# Revit family: 2M_Relief Valve_UNIVAL_URLV-0301 - 50-200 mm
name_source: partatom
category: Pipe Accessories
revit_build: Autodesk Revit 2016 (Build: 20150220_1215(x64)
units: mm (PartAtom-declared; Revit-internal decimal feet)

## family parameters
Always vertical = Yes
Cut with Voids When Loaded = No
OmniClass Number = 23.65.55.14
OmniClass Title = Valves for Liquid Services
Part Type = Valve - Breaks Into
Round Connector Dimension = Use Diameter
Shared = No
Work Plane-Based = No

## types (7) — shared parameters
Body Material = Ductile iron
Certifications = CE
Color = UNIVAL_Red
Connection Type = Flanged / Grooved
Description = Relief valve
Description TR = Relief vana
Disc Material = EPDM
Flanged = Yes
Grooved = No
Loss Method = Not Defined
Manufacturer = Giacomini Unival
Giacomini Unival
Giacomini Unival
Max. Working Temperature = 90°C
Pressure Rating = PN16 / PN25
URL = http://www.unival.com.tr

## per-type parameters (varying)
| type | D | DN | Elbow_D | Elbow_curve | Elbow_dist | Elbow_h | Ext_dist | Flange_w | H | H1 | Hexagon_d | Hexagon_h | Kv | L | Model | Profile2_x | Profile_d | Profile_y | Top_D |
| DN50 | 163 mm | 50 mm | 64 mm  [stored 0.209974 ft] | 120 mm | 89 mm | 60 mm  [stored 0.19685 ft] | 5 mm  [stored 0.0164042 ft] | 17 mm | 149 mm | 68 mm  [stored 0.223097 ft] | 63 mm  [stored 0.206693 ft] | 15 mm  [stored 0.0492126 ft] | 102 | 212 mm | URLV-0301X050 | 71 mm | 24 mm  [stored 0.0787402 ft] | 50 mm  [stored 0.164042 ft] | 32 mm  [stored 0.104987 ft] |
| DN65 | 184 mm | 65 mm | 65 mm  [stored 0.213255 ft] | 116 mm | 93 mm | 58 mm  [stored 0.190289 ft] | 5 mm  [stored 0.0164042 ft] | 17 mm | 154 mm | 66 mm  [stored 0.216535 ft] | 66 mm  [stored 0.216535 ft] | 15 mm  [stored 0.0492126 ft] | 102 | 220 mm | URLV-0301X065 | 73 mm  [stored 0.239501 ft] | 31 mm | 55 mm  [stored 0.180446 ft] | 33 mm  [stored 0.108268 ft] |
| DN80 | 204 mm | 80 mm | 80 mm  [stored 0.262467 ft] | 130 mm | 126 mm | 65 mm  [stored 0.213255 ft] | 33 mm  [stored 0.108268 ft] | 17 mm | 173 mm | 73 mm  [stored 0.239501 ft] | 80 mm  [stored 0.262467 ft] | 15 mm  [stored 0.0492126 ft] | 201 | 286 mm | URLV-0301X080 | 95 mm | 38 mm  [stored 0.124672 ft] | 62 mm  [stored 0.203412 ft] | 40 mm  [stored 0.131234 ft] |
| DN100 | 210 mm | 100 mm | 100 mm | 130 mm | 148 mm | 65 mm  [stored 0.213255 ft] | 40 mm  [stored 0.131234 ft] | 17 mm | 173 mm | 73 mm  [stored 0.239501 ft] | 100 mm | 15 mm  [stored 0.0492126 ft] | 216 | 330 mm | URLV-0301X100 | 110 mm | 48 mm  [stored 0.15748 ft] | 70 mm  [stored 0.229659 ft] | 50 mm  [stored 0.164042 ft] |
| DN125 | 262 mm | 125 mm | 125 mm | 160 mm | 167 mm | 80 mm  [stored 0.262467 ft] | 42 mm  [stored 0.137795 ft] | 17 mm | 212 mm | 88 mm  [stored 0.288714 ft] | 114 mm | 15 mm  [stored 0.0492126 ft] | 216 | 368 mm | URLV-0301X125 | 123 mm | 60 mm  [stored 0.19685 ft] | 86 mm  [stored 0.282152 ft] | 57 mm  [stored 0.187008 ft] |
| DN150 | 288 mm | 150 mm | 150 mm | 295 mm | 180 mm | 148 mm | 5 mm  [stored 0.0164042 ft] | 17 mm | 325 mm | 156 mm | 110 mm | 30 mm  [stored 0.0984252 ft] | 484 | 394 mm | URLV-0301X150 | 131 mm | 72 mm  [stored 0.23622 ft] | 100 mm | 55 mm  [stored 0.180446 ft] |
| DN200 | 350 mm | 200 mm | 200 mm | 360 mm | 213 mm | 180 mm | 6 mm  [stored 0.019685 ft] | 18 mm  [stored 0.0590551 ft] | 392 mm | 188 mm | 130 mm | 30 mm  [stored 0.0984252 ft] | 1316 | 462 mm | URLV-0301X200 | 154 mm | 120 mm | 114 mm | 65 mm  [stored 0.213255 ft] |

note: [stored X ft] marks values corroborated as IEEE doubles in the binary element streams (Revit-internal decimal feet)

## geometry (parser evidence)
native form markers: Sweep x5
no freeform markers — native parametric forms only
